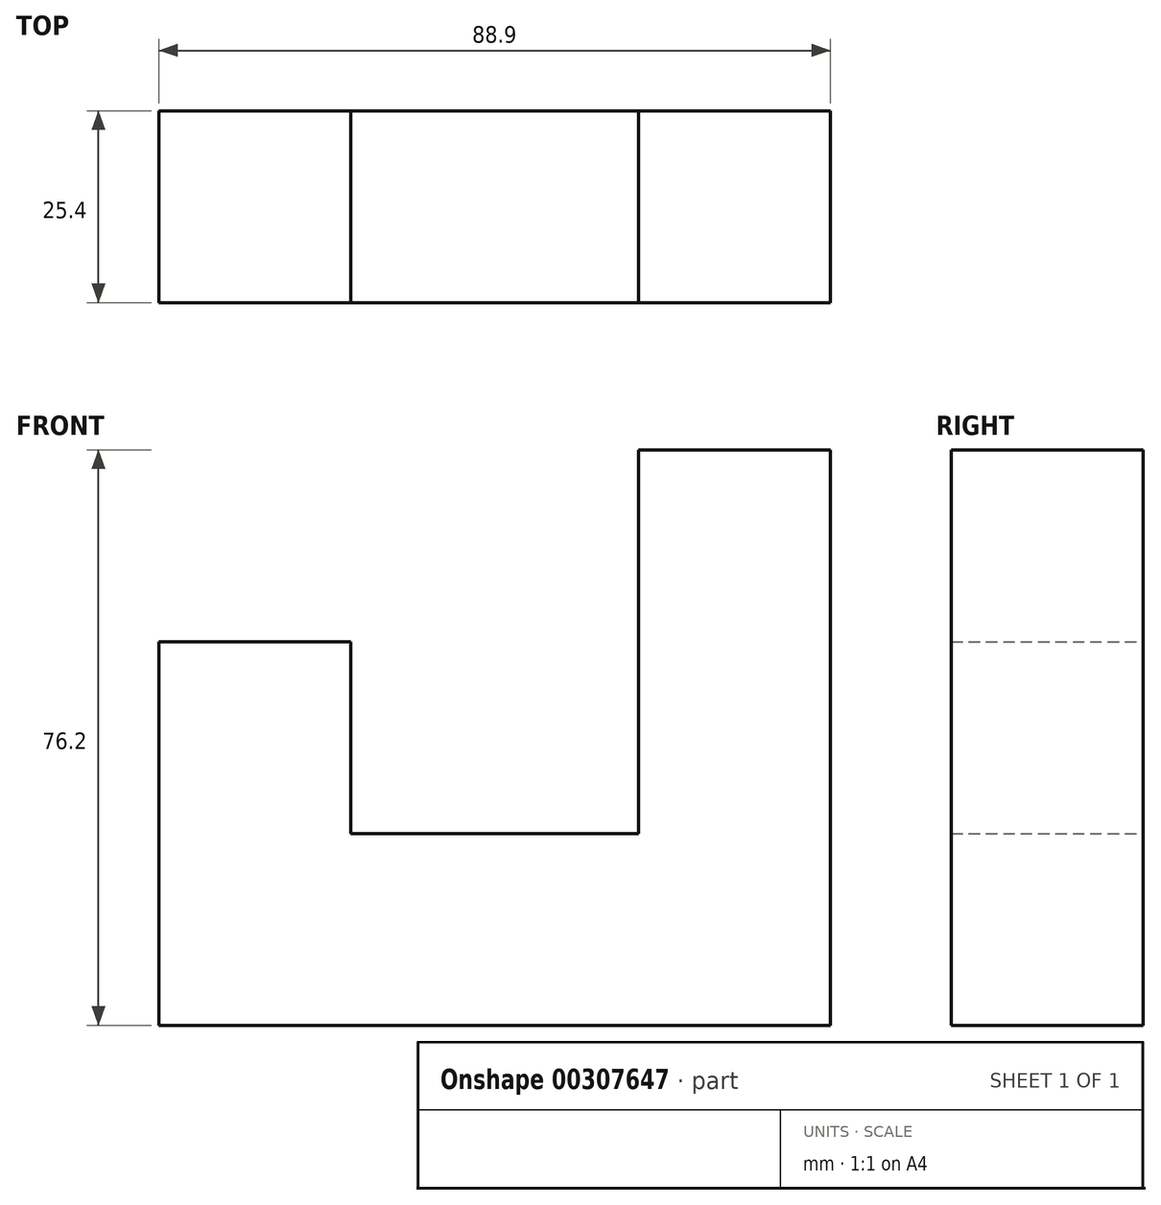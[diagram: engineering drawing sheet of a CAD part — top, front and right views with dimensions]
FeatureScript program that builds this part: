
annotation { "Feature Type Name" : "Feature", "Feature Type Description" : "" }
export const myFeature = defineFeature(function(context is Context, id is Id, definition is map)
    precondition{}
    {
        {
            var Q0;
            Q0=qCreatedBy(makeId("Front.planeOp"),FACE);
            var sketch = newSketch(context, id + "F0", { "sketchPlane" : qUnion([Q0])});
            skLineSegment(sketch, "E0", {"start": v(-39.37, -50.82) * mm, "end": v(49.53, -50.82) * mm});
            skLineSegment(sketch, "E1", {"start": v(49.53, -50.82) * mm, "end": v(49.53, 25.38) * mm});
            skLineSegment(sketch, "E2", {"start": v(49.53, 25.38) * mm, "end": v(24.13, 25.38) * mm});
            skLineSegment(sketch, "E3", {"start": v(24.13, 25.38) * mm, "end": v(24.13, -25.42) * mm});
            skLineSegment(sketch, "E4", {"start": v(24.13, -25.42) * mm, "end": v(-13.97, -25.42) * mm});
            skLineSegment(sketch, "E5", {"start": v(-13.97, -25.42) * mm, "end": v(-13.97, -0.02) * mm});
            skLineSegment(sketch, "E6", {"start": v(-13.97, -0.02) * mm, "end": v(-39.37, -0.02) * mm});
            skLineSegment(sketch, "E7", {"start": v(-39.37, -0.02) * mm, "end": v(-39.37, -50.82) * mm});
            skSolve(sketch);
        }
        {
            var Q0;
            Q0=makeQuery(id+"F0.imprint","IMPRINT",FACE,{"disambiguationData":[TD([[makeQuery(id+"F0.imprint","IMPRINT",EDGE,{"derivedFrom":sQuery(id+"F0.wireOp",EDGE,"E0")}),1.0]])]});
            extrude(context, id + "F1", {"entities" : qUnion([Q0]), "depth" : 25.4 * mm});
        }
    });
